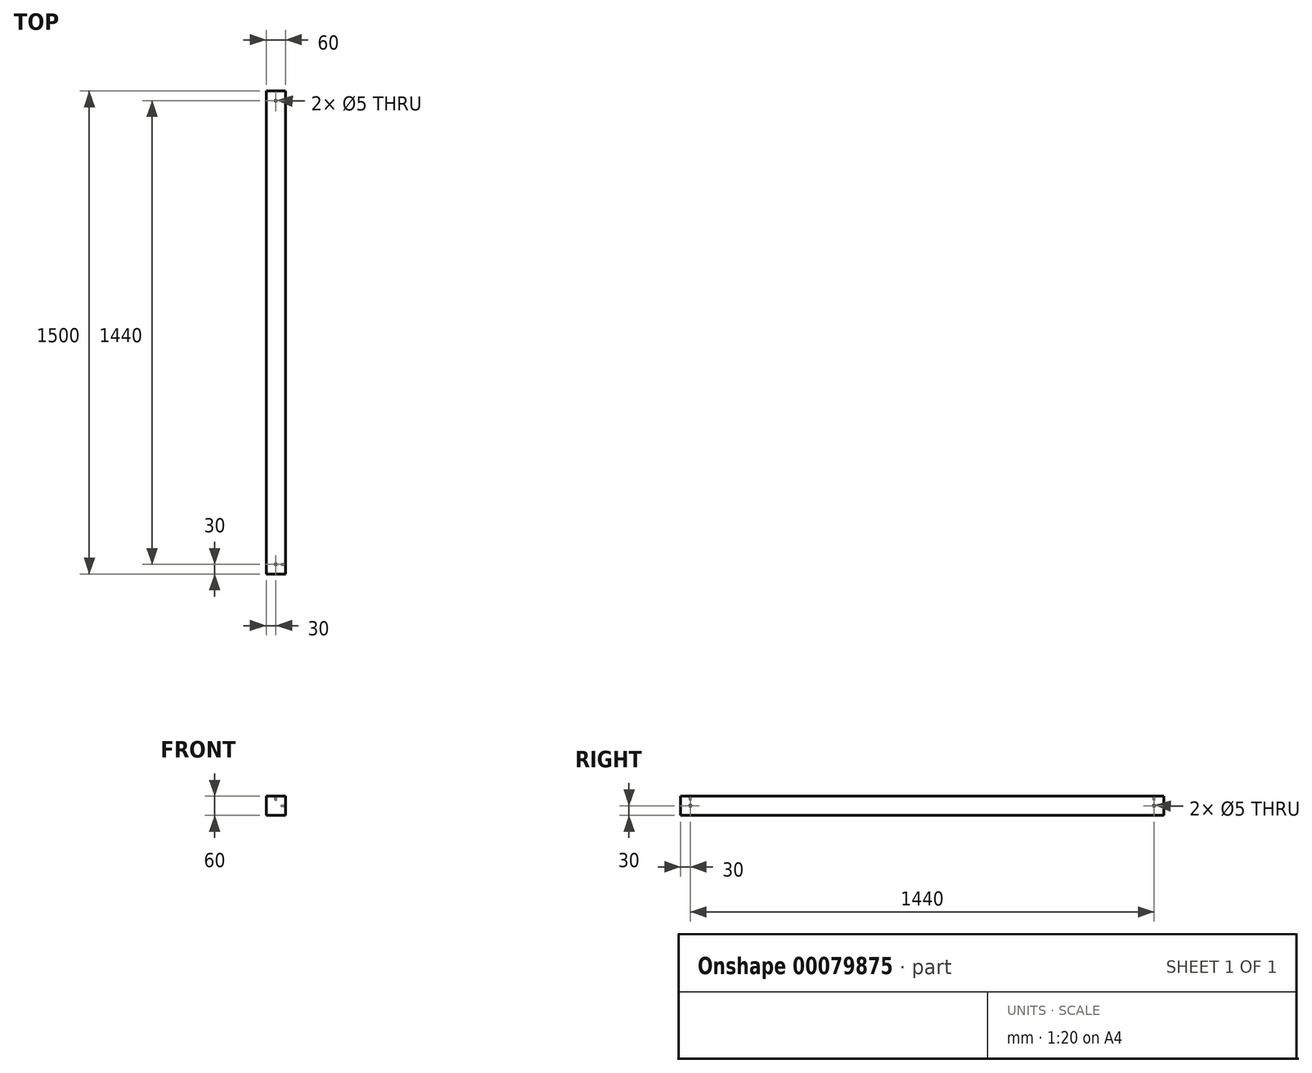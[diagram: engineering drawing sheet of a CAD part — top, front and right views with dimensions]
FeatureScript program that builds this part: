
annotation { "Feature Type Name" : "Feature", "Feature Type Description" : "" }
export const myFeature = defineFeature(function(context is Context, id is Id, definition is map)
    precondition{}
    {
        {
            assignVariable(context, id + "F0", {"name" : "bed_length", "anyValue" : 1500 * mm});
        }
        {
            assignVariable(context, id + "F1", {"name" : "hole_diameter", "anyValue" : 5});
        }
        {
            assignVariable(context, id + "F2", {"name" : "hole_length", "anyValue" : 12});
        }
        {
            var Q0;
            Q0=qCreatedBy(makeId("Front.planeOp"),FACE);
            var sketch = newSketch(context, id + "F3", { "sketchPlane" : qUnion([Q0])});
            skLineSegment(sketch, "E0.bottom", {"start": v(0, 0) * mm, "end": v(60, 0) * mm});
            skLineSegment(sketch, "E0.top", {"start": v(0, 60) * mm, "end": v(60, 60) * mm});
            skLineSegment(sketch, "E0.left", {"start": v(0, 0) * mm, "end": v(0, 60) * mm});
            skLineSegment(sketch, "E0.right", {"start": v(60, 0) * mm, "end": v(60, 60) * mm});
            skSolve(sketch);
        }
        {
            var Q0;
            Q0=makeQuery(id+"F3.imprint","IMPRINT",FACE,{"disambiguationData":[TD([[makeQuery(id+"F3.imprint","IMPRINT",EDGE,{"derivedFrom":sQuery(id+"F3.wireOp",EDGE,"E0.bottom")}),1.0]])]});
            extrude(context, id + "F4", {"entities" : qUnion([Q0]), "depth" : getVariable(context, 'bed_length')});
        }
        {
            var Q0;
            Q0=makeQuery(id+"F4.opExtrude","SWEPT_FACE",FACE,{"disambiguationData":[OSD([sQuery(id+"F3.wireOp",EDGE,"E0.top")])]});
            var sketch = newSketch(context, id + "F5", { "sketchPlane" : qUnion([Q0])});
            skPoint(sketch, "E1", {"position": v(30, -1470) * mm});
            skPoint(sketch, "E1.positionSnap0", {"position": v(30, -1500) * mm});
            skPoint(sketch, "E2", {"position": v(30, -30) * mm});
            skPoint(sketch, "E2.positionSnap0", {"position": v(30, 0) * mm});
            skSolve(sketch);
        }
        {
            var Q0;
            Q0=makeQuery(id+"F4.opExtrude","SWEPT_FACE",FACE,{"disambiguationData":[OSD([sQuery(id+"F3.wireOp",EDGE,"E0.right")])]});
            var sketch = newSketch(context, id + "F6", { "sketchPlane" : qUnion([Q0])});
            skPoint(sketch, "E3", {"position": v(-1470, 30) * mm});
            skPoint(sketch, "E3.positionSnap0", {"position": v(-1500, 30) * mm});
            skPoint(sketch, "E4", {"position": v(-30, 30) * mm});
            skPoint(sketch, "E4.positionSnap0", {"position": v(0, 30) * mm});
            skSolve(sketch);
        }
        {
            var Q0;
            Q0=sQuery(id+"F5.wireOp",VERTEX,"E1");
            var Q1;
            Q1=sQuery(id+"F5.wireOp",VERTEX,"E2");
            var Q2;
            Q2=makeQuery(id+"F4.opExtrude","SWEPT_BODY",BODY,{"disambiguationData":[OSD([sQuery(id+"F3.wireOp",EDGE,"E0.bottom"),sQuery(id+"F3.wireOp",EDGE,"E0.top"),sQuery(id+"F3.wireOp",EDGE,"E0.left"),sQuery(id+"F3.wireOp",EDGE,"E0.right")])]});
            hole(context, id + "F7", {"style" : HoleStyle.SIMPLE, "endStyle" : HoleEndStyle.BLIND, "holeDiameter" : (getVariable(context, 'hole_diameter')) * mm, "holeDepth" : (getVariable(context, 'hole_length')) * mm, "locations" : qUnion([Q0, Q1]), "scope" : qUnion([Q2])});
        }
        {
            var Q0;
            Q0=sQuery(id+"F6.wireOp",VERTEX,"E4");
            var Q1;
            Q1=sQuery(id+"F6.wireOp",VERTEX,"E3");
            var Q2;
            Q2=makeQuery(id+"F4.opExtrude","SWEPT_BODY",BODY,{"disambiguationData":[OSD([sQuery(id+"F3.wireOp",EDGE,"E0.bottom"),sQuery(id+"F3.wireOp",EDGE,"E0.top"),sQuery(id+"F3.wireOp",EDGE,"E0.left"),sQuery(id+"F3.wireOp",EDGE,"E0.right")])]});
            hole(context, id + "F8", {"style" : HoleStyle.SIMPLE, "endStyle" : HoleEndStyle.BLIND, "holeDiameter" : (getVariable(context, 'hole_diameter')) * mm, "holeDepth" : (getVariable(context, 'hole_length')) * mm, "startFromSketch" : true, "locations" : qUnion([Q0, Q1]), "scope" : qUnion([Q2])});
        }
    });
